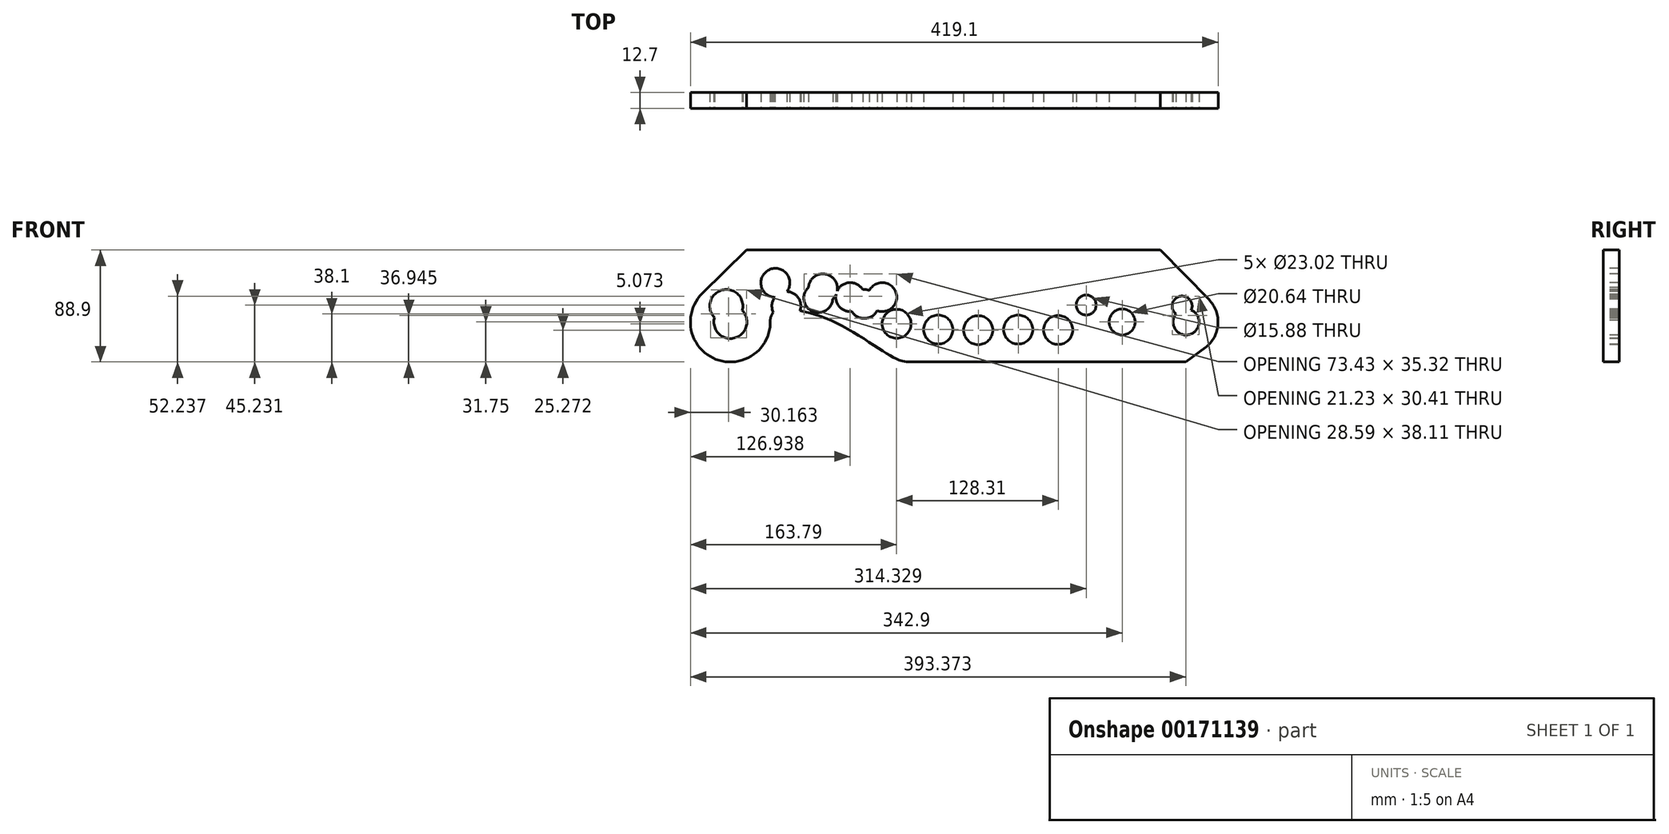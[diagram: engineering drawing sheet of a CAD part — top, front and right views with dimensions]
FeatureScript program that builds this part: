
annotation { "Feature Type Name" : "Feature", "Feature Type Description" : "" }
export const myFeature = defineFeature(function(context is Context, id is Id, definition is map)
    precondition{}
    {
        {
            var Q0;
            Q0=qCreatedBy(makeId("Front.planeOp"),FACE);
            var sketch = newSketch(context, id + "F0", { "sketchPlane" : qUnion([Q0])});
            skLineSegment(sketch, "E0.bottom", {"start": v(-209.55, 44.45) * mm, "end": v(209.55, 44.45) * mm});
            skLineSegment(sketch, "E0.top", {"start": v(-209.55, -44.45) * mm, "end": v(209.55, -44.45) * mm});
            skLineSegment(sketch, "E0.left", {"start": v(-209.55, 44.45) * mm, "end": v(-209.55, -44.45) * mm});
            skLineSegment(sketch, "E0.right", {"start": v(209.55, 44.45) * mm, "end": v(209.55, -44.45) * mm});
            skPoint(sketch, "E0.middle", {"position": v(0, 0) * mm});
            skCircle(sketch, "E1", {"center": v(-177.8, -12.7) * mm, "radius": 13.1 * mm});
            skLineSegment(sketch, "E2", {"start": v(228.8, -12.7) * mm, "end": v(86.37, -12.7) * mm, "construction": true});
            skCircle(sketch, "E3", {"center": v(184.15, -12.7) * mm, "radius": 10.32 * mm});
            skCircle(sketch, "E4", {"center": v(133.35, -12.7) * mm, "radius": 10.32 * mm});
            skLineSegment(sketch, "E5", {"start": v(121.2, -19.05) * mm, "end": v(-51.15, -19.05) * mm, "construction": true});
            skCircle(sketch, "E6", {"center": v(82.55, -19.05) * mm, "radius": 11.5 * mm});
            skCircle(sketch, "E7", {"center": v(50.8, -18.73) * mm, "radius": 11.5 * mm});
            skCircle(sketch, "E8", {"center": v(19.05, -19.18) * mm, "radius": 11.5 * mm});
            skCircle(sketch, "E9", {"center": v(-12.7, -18.73) * mm, "radius": 11.5 * mm});
            skSolve(sketch);
        }
        {
            var Q0;
            Q0=makeQuery(id+"F0.imprint","IMPRINT",FACE,{"disambiguationData":[TD([[makeQuery(id+"F0.imprint","IMPRINT",EDGE,{"derivedFrom":sQuery(id+"F0.wireOp",EDGE,"E0.bottom")}),-1.0]])]});
            extrude(context, id + "F1", {"entities" : qUnion([Q0]), "oppositeDirection" : true, "depth" : 12.7 * mm});
        }
        {
            var Q0;
            Q0=makeQuery(id+"F1.opExtrude","CAP_FACE",FACE,{"disambiguationData":[OSD([sQuery(id+"F0.wireOp",EDGE,"E0.bottom"),sQuery(id+"F0.wireOp",EDGE,"E0.top"),sQuery(id+"F0.wireOp",EDGE,"E0.left"),sQuery(id+"F0.wireOp",EDGE,"E0.right"),sQuery(id+"F0.wireOp",EDGE,"E1"),sQuery(id+"F0.wireOp",EDGE,"E3"),sQuery(id+"F0.wireOp",EDGE,"E4"),sQuery(id+"F0.wireOp",EDGE,"E6"),sQuery(id+"F0.wireOp",EDGE,"E7"),sQuery(id+"F0.wireOp",EDGE,"E8"),sQuery(id+"F0.wireOp",EDGE,"E9")])],"isStart":true});
            var sketch = newSketch(context, id + "F2", { "sketchPlane" : qUnion([Q0])});
            skLineSegment(sketch, "E10", {"start": v(-177.73, 37.77) * mm, "end": v(-177.73, -158.75) * mm, "construction": true});
            skLineSegment(sketch, "E11", {"start": v(-177.8, -12.7) * mm, "end": v(-109.95, -12.7) * mm, "construction": true});
            skLineSegment(sketch, "E12", {"start": v(-177.73, -158.75) * mm, "end": v(-149.16, -158.75) * mm, "construction": true});
            skArc(sketch, "E13", {"start": v(-193.34, 13.47) * mm, "mid": v(-92.02, 9.62) * mm, "end": v(-9.28, -48.99) * mm, "construction": true});
            skCircle(sketch, "E14", {"center": v(-45.76, -14.1) * mm, "radius": 11.5 * mm});
            skCircle(sketch, "E15", {"center": v(-71.52, 1.63) * mm, "radius": 11.5 * mm});
            skCircle(sketch, "E16", {"center": v(-104.3, 14.02) * mm, "radius": 11.5 * mm});
            skCircle(sketch, "E17", {"center": v(-142.08, 18.42) * mm, "radius": 11.5 * mm});
            skSolve(sketch);
        }
        {
            var Q0;
            Q0=makeQuery(id+"F2.imprint","IMPRINT",FACE,{"disambiguationData":[TD([[makeQuery(id+"F2.imprint","IMPRINT",EDGE,{"derivedFrom":sQuery(id+"F2.wireOp",EDGE,"E17")}),1.0]])]});
            var Q1;
            Q1=makeQuery(id+"F2.imprint","IMPRINT",FACE,{"disambiguationData":[TD([[makeQuery(id+"F2.imprint","IMPRINT",EDGE,{"derivedFrom":sQuery(id+"F2.wireOp",EDGE,"E16")}),1.0]])]});
            var Q2;
            Q2=makeQuery(id+"F2.imprint","IMPRINT",FACE,{"disambiguationData":[TD([[makeQuery(id+"F2.imprint","IMPRINT",EDGE,{"derivedFrom":sQuery(id+"F2.wireOp",EDGE,"E15")}),1.0]])]});
            var Q3;
            Q3=makeQuery(id+"F2.imprint","IMPRINT",FACE,{"disambiguationData":[TD([[makeQuery(id+"F2.imprint","IMPRINT",EDGE,{"derivedFrom":sQuery(id+"F2.wireOp",EDGE,"E14")}),1.0]])]});
            extrude(context, id + "F3", {"entities" : qUnion([Q0, Q1, Q2, Q3]), "operationType" : NewBodyOperationType.REMOVE, "endBound" : BoundingType.THROUGH_ALL, "oppositeDirection" : true, "depth" : 25.4 * mm});
        }
        {
            var Q0;
            Q0=makeQuery(id+"F1.opExtrude","CAP_FACE",FACE,{"disambiguationData":[OSD([sQuery(id+"F0.wireOp",EDGE,"E0.bottom"),sQuery(id+"F0.wireOp",EDGE,"E0.top"),sQuery(id+"F0.wireOp",EDGE,"E0.left"),sQuery(id+"F0.wireOp",EDGE,"E0.right"),sQuery(id+"F0.wireOp",EDGE,"E1"),sQuery(id+"F0.wireOp",EDGE,"E3"),sQuery(id+"F0.wireOp",EDGE,"E4"),sQuery(id+"F0.wireOp",EDGE,"E6"),sQuery(id+"F0.wireOp",EDGE,"E7"),sQuery(id+"F0.wireOp",EDGE,"E8"),sQuery(id+"F0.wireOp",EDGE,"E9")])],"isStart":true});
            var sketch = newSketch(context, id + "F4", { "sketchPlane" : qUnion([Q0])});
            skCircle(sketch, "E18", {"center": v(-177.8, -12.7) * mm, "radius": 31.75 * mm});
            skLineSegment(sketch, "E19", {"start": v(-165.1, 44.45) * mm, "end": v(-200.1, 9.9) * mm});
            skLineSegment(sketch, "E20", {"start": v(-146.05, -65.48) * mm, "end": v(-146.05, 3.2) * mm, "construction": true});
            skArc(sketch, "E21", {"start": v(-146.05, -12.7) * mm, "mid": v(-143.4, -4.8) * mm, "end": v(-135.73, -1.54) * mm});
            skFitSpline(sketch, "E22", {"points": [v(-135.73, -1.54) * mm, v(-97.75, -11.51) * mm, v(-55.1, -36.8) * mm, v(-38.1, -44.45) * mm], "startDerivative": vector(106.71, -14.43) * mm, "endDerivative": vector(80.2, -15.75) * mm});
            skSolve(sketch);
        }
        {
            var Q0;
            {var subQ0=sQuery(id+"F4.wireOp",EDGE,"E19");Q0=makeQuery(id+"F4.imprint","IMPRINT",FACE,{"disambiguationData":[TD([[makeQuery(id+"F4.imprint","IMPRINT",EDGE,{"derivedFrom":subQ0}),-1.0]])]});}
            var Q1;
            {var subQ0=sQuery(id+"F4.wireOp",EDGE,"E18");var subQ1=makeQuery(id+"F1.opExtrude","CAP_EDGE",EDGE,{"disambiguationData":[OSD([sQuery(id+"F0.wireOp",EDGE,"E0.left")])],"isStart":true});var subQ2=makeQuery(id+"F4.imprint","INTERSECT",VERTEX,{"derivedFrom":[subQ1,subQ0]});Q1=makeQuery(id+"F4.imprint","IMPRINT",FACE,{"disambiguationData":[TD([[makeQuery(id+"F4.imprint","IMPRINT",EDGE,{"disambiguationData":[TD([[subQ2,-1.0]])],"derivedFrom":subQ0}),-1.0]])]});}
            var Q2;
            {var subQ0=sQuery(id+"F4.wireOp",EDGE,"E22");Q2=makeQuery(id+"F4.imprint","IMPRINT",FACE,{"disambiguationData":[TD([[makeQuery(id+"F4.imprint","IMPRINT",EDGE,{"derivedFrom":subQ0}),-1.0]])]});}
            extrude(context, id + "F5", {"entities" : qUnion([Q0, Q1, Q2]), "operationType" : NewBodyOperationType.REMOVE, "endBound" : BoundingType.THROUGH_ALL, "oppositeDirection" : true, "depth" : 25.4 * mm});
        }
        {
            var Q0;
            Q0=makeQuery(id+"F1.opExtrude","CAP_FACE",FACE,{"disambiguationData":[OSD([sQuery(id+"F0.wireOp",EDGE,"E0.bottom"),sQuery(id+"F0.wireOp",EDGE,"E0.top"),sQuery(id+"F0.wireOp",EDGE,"E0.left"),sQuery(id+"F0.wireOp",EDGE,"E0.right"),sQuery(id+"F0.wireOp",EDGE,"E1"),sQuery(id+"F0.wireOp",EDGE,"E3"),sQuery(id+"F0.wireOp",EDGE,"E4"),sQuery(id+"F0.wireOp",EDGE,"E6"),sQuery(id+"F0.wireOp",EDGE,"E7"),sQuery(id+"F0.wireOp",EDGE,"E8"),sQuery(id+"F0.wireOp",EDGE,"E9")])],"isStart":true});
            var sketch = newSketch(context, id + "F6", { "sketchPlane" : qUnion([Q0])});
            skLineSegment(sketch, "E23", {"start": v(163.51, 44.45) * mm, "end": v(202.25, 5.12) * mm});
            skArc(sketch, "E24", {"start": v(199.4, -33.02) * mm, "mid": v(209.48, -14.6) * mm, "end": v(202.25, 5.12) * mm});
            skLineSegment(sketch, "E25", {"start": v(184.15, -44.45) * mm, "end": v(199.4, -33.02) * mm});
            skSolve(sketch);
        }
        {
            var Q0;
            {var subQ0=sQuery(id+"F6.wireOp",EDGE,"E23");Q0=makeQuery(id+"F6.imprint","IMPRINT",FACE,{"disambiguationData":[TD([[makeQuery(id+"F6.imprint","IMPRINT",EDGE,{"derivedFrom":subQ0}),1.0]])]});}
            var Q1;
            {var subQ0=sQuery(id+"F6.wireOp",EDGE,"E25");Q1=makeQuery(id+"F6.imprint","IMPRINT",FACE,{"disambiguationData":[TD([[makeQuery(id+"F6.imprint","IMPRINT",EDGE,{"derivedFrom":subQ0}),-1.0]])]});}
            extrude(context, id + "F7", {"entities" : qUnion([Q0, Q1]), "operationType" : NewBodyOperationType.REMOVE, "endBound" : BoundingType.THROUGH_ALL, "oppositeDirection" : true, "depth" : 25.4 * mm});
        }
        {
            var Q0;
            Q0=qCreatedBy(makeId("Front.planeOp"),FACE);
            var sketch = newSketch(context, id + "F8", { "sketchPlane" : qUnion([Q0])});
            skLineSegment(sketch, "E26.bottom", {"start": v(-180.98, 31.75) * mm, "end": v(180.97, 31.75) * mm});
            skLineSegment(sketch, "E26.top", {"start": v(-180.98, -31.75) * mm, "end": v(180.97, -31.75) * mm});
            skPoint(sketch, "E26.middle", {"position": v(0, 0) * mm});
            skArc(sketch, "E27", {"start": v(-180.98, 31.75) * mm, "mid": v(-212.73, 0) * mm, "end": v(-180.98, -31.75) * mm});
            skArc(sketch, "E28", {"start": v(180.98, -31.75) * mm, "mid": v(212.73, 0) * mm, "end": v(180.98, 31.75) * mm});
            skPoint(sketch, "E29.orphan", {"position": v(-212.73, 31.75) * mm});
            skPoint(sketch, "E30.orphan", {"position": v(-212.73, -31.75) * mm});
            skPoint(sketch, "E31.orphan", {"position": v(212.72, 31.75) * mm});
            skPoint(sketch, "E32.orphan", {"position": v(212.72, -31.75) * mm});
            skSolve(sketch);
        }
        {
            var Q0;
            Q0=makeQuery(id+"F8.imprint","IMPRINT",FACE,{"disambiguationData":[TD([[makeQuery(id+"F8.imprint","IMPRINT",EDGE,{"derivedFrom":sQuery(id+"F8.wireOp",EDGE,"E26.bottom")}),-1.0]])]});
            extrude(context, id + "F9", {"entities" : qUnion([Q0]), "depth" : 12.7 * mm});
        }
        {
            var Q0;
            Q0=makeQuery(id+"F9.opExtrude","CAP_FACE",FACE,{"disambiguationData":[OSD([sQuery(id+"F8.wireOp",EDGE,"E26.bottom"),sQuery(id+"F8.wireOp",EDGE,"E26.top"),sQuery(id+"F8.wireOp",EDGE,"E27"),sQuery(id+"F8.wireOp",EDGE,"E28")])],"isStart":false});
            var sketch = newSketch(context, id + "F10", { "sketchPlane" : qUnion([Q0])});
            skCircle(sketch, "E33", {"center": v(-180.98, 0) * mm, "radius": 13.1 * mm});
            skCircle(sketch, "E34", {"center": v(-133.35, 0) * mm, "radius": 11.5 * mm});
            skLineSegment(sketch, "E35", {"start": v(-115.23, 6.35) * mm, "end": v(-36.78, 6.35) * mm, "construction": true});
            skCircle(sketch, "E36", {"center": v(-107.95, 6.35) * mm, "radius": 11.5 * mm});
            skCircle(sketch, "E37", {"center": v(-82.55, 7.09) * mm, "radius": 11.5 * mm});
            skCircle(sketch, "E38", {"center": v(-57.15, 7.09) * mm, "radius": 11.5 * mm});
            skCircle(sketch, "E39", {"center": v(180.98, 0) * mm, "radius": 7.94 * mm});
            skCircle(sketch, "E40", {"center": v(104.78, 0.78) * mm, "radius": 7.94 * mm});
            skSolve(sketch);
        }
        {
            var Q0;
            Q0=makeQuery(id+"F10.imprint","IMPRINT",FACE,{"disambiguationData":[TD([[makeQuery(id+"F10.imprint","IMPRINT",EDGE,{"derivedFrom":sQuery(id+"F10.wireOp",EDGE,"E33")}),1.0]])]});
            var Q1;
            Q1=makeQuery(id+"F10.imprint","IMPRINT",FACE,{"disambiguationData":[TD([[makeQuery(id+"F10.imprint","IMPRINT",EDGE,{"derivedFrom":sQuery(id+"F10.wireOp",EDGE,"E34")}),1.0]])]});
            var Q2;
            Q2=makeQuery(id+"F10.imprint","IMPRINT",FACE,{"disambiguationData":[TD([[makeQuery(id+"F10.imprint","IMPRINT",EDGE,{"derivedFrom":sQuery(id+"F10.wireOp",EDGE,"E36")}),1.0]])]});
            var Q3;
            Q3=makeQuery(id+"F10.imprint","IMPRINT",FACE,{"disambiguationData":[TD([[makeQuery(id+"F10.imprint","IMPRINT",EDGE,{"derivedFrom":sQuery(id+"F10.wireOp",EDGE,"E37")}),1.0]])]});
            var Q4;
            Q4=makeQuery(id+"F10.imprint","IMPRINT",FACE,{"disambiguationData":[TD([[makeQuery(id+"F10.imprint","IMPRINT",EDGE,{"derivedFrom":sQuery(id+"F10.wireOp",EDGE,"E38")}),1.0]])]});
            var Q5;
            Q5=makeQuery(id+"F10.imprint","IMPRINT",FACE,{"disambiguationData":[TD([[makeQuery(id+"F10.imprint","IMPRINT",EDGE,{"derivedFrom":sQuery(id+"F10.wireOp",EDGE,"E40")}),1.0]])]});
            var Q6;
            Q6=makeQuery(id+"F10.imprint","IMPRINT",FACE,{"disambiguationData":[TD([[makeQuery(id+"F10.imprint","IMPRINT",EDGE,{"derivedFrom":sQuery(id+"F10.wireOp",EDGE,"E39")}),1.0]])]});
            extrude(context, id + "F11", {"entities" : qUnion([Q0, Q1, Q2, Q3, Q4, Q5, Q6]), "operationType" : NewBodyOperationType.REMOVE, "endBound" : BoundingType.THROUGH_ALL, "oppositeDirection" : true, "depth" : 25.4 * mm});
        }
        {
            var Q0;
            Q0=makeQuery(id+"F9.opExtrude","SWEPT_BODY",BODY,{"disambiguationData":[OSD([sQuery(id+"F8.wireOp",EDGE,"E26.bottom"),sQuery(id+"F8.wireOp",EDGE,"E26.top"),sQuery(id+"F8.wireOp",EDGE,"E27"),sQuery(id+"F8.wireOp",EDGE,"E28")])]});
            deleteBodies(context, id + "F12", {"entities" : qUnion([Q0])});
        }
    });
